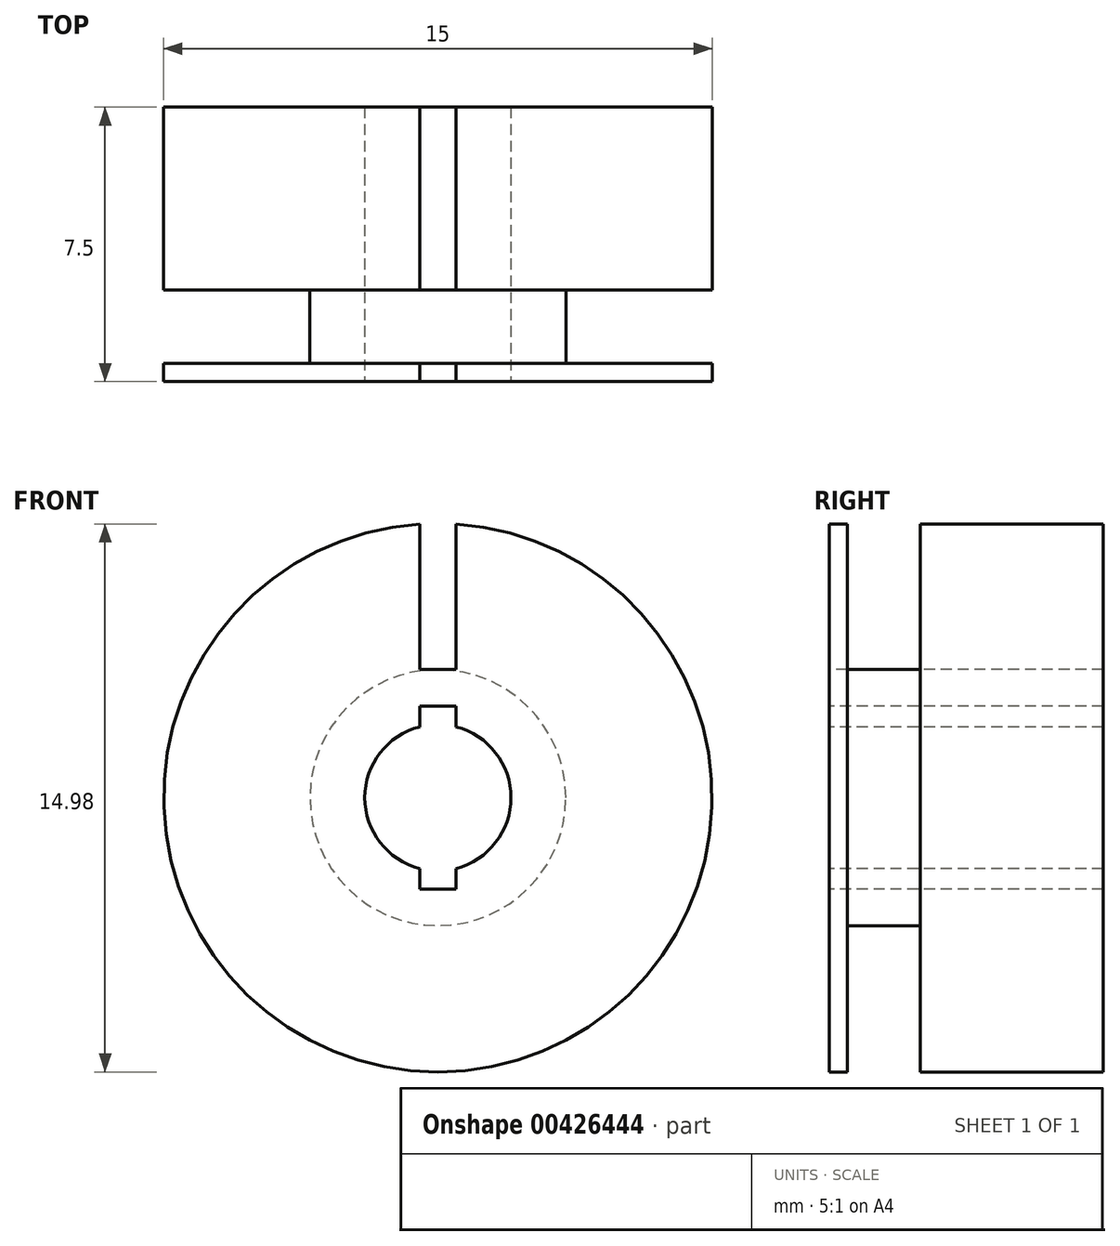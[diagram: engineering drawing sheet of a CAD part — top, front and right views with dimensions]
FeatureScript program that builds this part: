
annotation { "Feature Type Name" : "Feature", "Feature Type Description" : "" }
export const myFeature = defineFeature(function(context is Context, id is Id, definition is map)
    precondition{}
    {
        {
            var Q0;
            Q0=qCreatedBy(makeId("Right.planeOp"),FACE);
            var sketch = newSketch(context, id + "F0", { "sketchPlane" : qUnion([Q0])});
            skLineSegment(sketch, "E0", {"start": v(10.2, 7.5) * mm, "end": v(10.2, 3.5) * mm});
            skLineSegment(sketch, "E1", {"start": v(10.2, 3.5) * mm, "end": v(8.2, 3.5) * mm});
            skLineSegment(sketch, "E2", {"start": v(8.2, 3.5) * mm, "end": v(8.2, 7.5) * mm});
            skLineSegment(sketch, "E3.trimOffspring", {"start": v(7.7, 7.5) * mm, "end": v(8.2, 7.5) * mm});
            skLineSegment(sketch, "E4.trimOffspring", {"start": v(10.2, 7.5) * mm, "end": v(10.2, 7.5) * mm});
            skLineSegment(sketch, "E5", {"start": v(10.2, 7.5) * mm, "end": v(15.2, 7.5) * mm});
            skLineSegment(sketch, "E6", {"start": v(15.2, 7.5) * mm, "end": v(15.2, 2) * mm});
            skLineSegment(sketch, "E7", {"start": v(7.7, 7.5) * mm, "end": v(7.7, 2) * mm});
            skLineSegment(sketch, "E8.trimOffspring", {"start": v(15.2, 0) * mm, "end": v(50.56, 0) * mm, "construction": true});
            skPoint(sketch, "E9.orphan", {"position": v(7.2, 7.5) * mm});
            skPoint(sketch, "E10.end.orphan", {"position": v(-10.3, 0) * mm});
            skPoint(sketch, "E10.start.orphan", {"position": v(-25, 0) * mm});
            skLineSegment(sketch, "E11", {"start": v(7.7, 2) * mm, "end": v(15.2, 2) * mm});
            skPoint(sketch, "E12.start.orphan", {"position": v(7.7, 0) * mm});
            skSolve(sketch);
        }
        {
            var Q0;
            Q0 = qSketchRegion(id + "F0", true);
            var Q1;
            Q1=sQuery(id+"F0.wireOp",EDGE,"E8.trimOffspring");
            revolve(context, id + "F1", {"entities" : qUnion([Q0]), "axis" : qUnion([Q1]), "revolveType" : RevolveType.FULL});
        }
        {
            var Q0;
            Q0=makeQuery(id+"F1.opRevolve","SWEPT_FACE",FACE,{"disambiguationData":[OSD([sQuery(id+"F0.wireOp",EDGE,"E7")])]});
            var sketch = newSketch(context, id + "F2", { "sketchPlane" : qUnion([Q0])});
            skLineSegment(sketch, "E13.bottom", {"start": v(-0.5, 11.5) * mm, "end": v(0.5, 11.5) * mm});
            skLineSegment(sketch, "E13.top", {"start": v(-0.5, 3.5) * mm, "end": v(0.5, 3.5) * mm});
            skLineSegment(sketch, "E13.left", {"start": v(-0.5, 11.5) * mm, "end": v(-0.5, 3.5) * mm});
            skLineSegment(sketch, "E13.right", {"start": v(0.5, 11.5) * mm, "end": v(0.5, 3.5) * mm});
            skPoint(sketch, "E13.middle", {"position": v(0, 7.5) * mm});
            skSolve(sketch);
        }
        {
            var Q0;
            Q0 = qSketchRegion(id + "F2", true);
            extrude(context, id + "F3", {"entities" : qUnion([Q0]), "operationType" : NewBodyOperationType.REMOVE, "oppositeDirection" : true, "depth" : 25 * mm});
        }
        {
            var Q0;
            Q0=makeQuery(id+"F1.opRevolve","SWEPT_FACE",FACE,{"disambiguationData":[OSD([sQuery(id+"F0.wireOp",EDGE,"E7")])]});
            var sketch = newSketch(context, id + "F4", { "sketchPlane" : qUnion([Q0])});
            skLineSegment(sketch, "E14.bottom", {"start": v(-0.5, -1.5) * mm, "end": v(0.5, -1.5) * mm});
            skLineSegment(sketch, "E14.top", {"start": v(-0.5, -2.5) * mm, "end": v(0.5, -2.5) * mm});
            skLineSegment(sketch, "E14.left", {"start": v(-0.5, -1.5) * mm, "end": v(-0.5, -2.5) * mm});
            skLineSegment(sketch, "E14.right", {"start": v(0.5, -1.5) * mm, "end": v(0.5, -2.5) * mm});
            skPoint(sketch, "E14.middle", {"position": v(0, -2) * mm});
            skLineSegment(sketch, "E15.bottom", {"start": v(-0.5, 2.5) * mm, "end": v(0.5, 2.5) * mm});
            skLineSegment(sketch, "E15.top", {"start": v(-0.5, 1.5) * mm, "end": v(0.5, 1.5) * mm});
            skLineSegment(sketch, "E15.left", {"start": v(-0.5, 2.5) * mm, "end": v(-0.5, 1.5) * mm});
            skLineSegment(sketch, "E15.right", {"start": v(0.5, 2.5) * mm, "end": v(0.5, 1.5) * mm});
            skPoint(sketch, "E15.middle", {"position": v(0, 2) * mm});
            skSolve(sketch);
        }
        {
            var Q0;
            Q0 = qSketchRegion(id + "F4", true);
            extrude(context, id + "F5", {"entities" : qUnion([Q0]), "operationType" : NewBodyOperationType.REMOVE, "oppositeDirection" : true, "depth" : 25 * mm});
        }
    });
